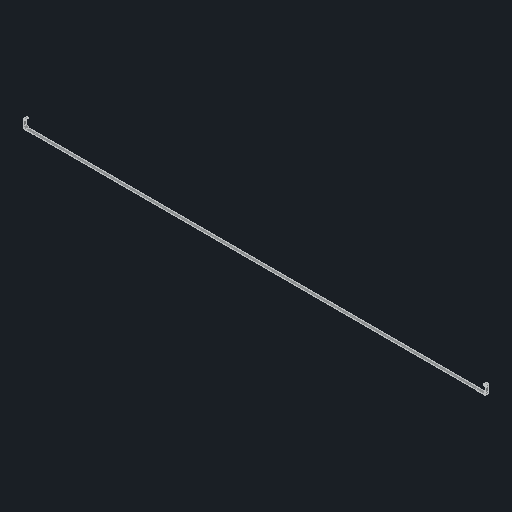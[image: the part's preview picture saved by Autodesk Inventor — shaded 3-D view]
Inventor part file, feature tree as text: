
AUTODESK INVENTOR PART (.ipt)
format: ipt  version: 2025 (Build 290162000, 162)  size: 131,584 bytes
history: native  units: in
note: dims shown in document units (in); Inventor stores cm internally (conversion verified against a paired STEP export)
features: mirror x1
ambient origin geometry x8: Origin, YZ Plane, XZ Plane, XY Plane, X Axis, Y Axis, Z Axis, Center Point
bodies: Solid1 (feature_tree)
feature tree (1):
  mirror  "Mirror1"
